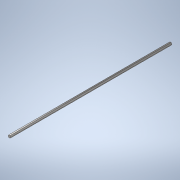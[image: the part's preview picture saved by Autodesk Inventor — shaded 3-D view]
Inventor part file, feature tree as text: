
AUTODESK INVENTOR PART (.ipt)
format: ipt  version: 2020 (Build 240168000, 168)  size: 110,080 bytes
history: native  units: in
note: dims shown in document units (in); Inventor stores cm internally (conversion verified against a paired STEP export)
features: extrude x1, sketch x1
ambient origin geometry x8: Origin, YZ Plane, XZ Plane, XY Plane, X Axis, Y Axis, Z Axis, Center Point
bodies: Solid1 (feature_tree)
feature tree (2):
  extrude  "Extrusion1"  Depth=35.0in TaperAngle=0.0deg
  sketch  "Sketch1"  dims[d0=0.5in d1=35.0in d2=0.0in]
